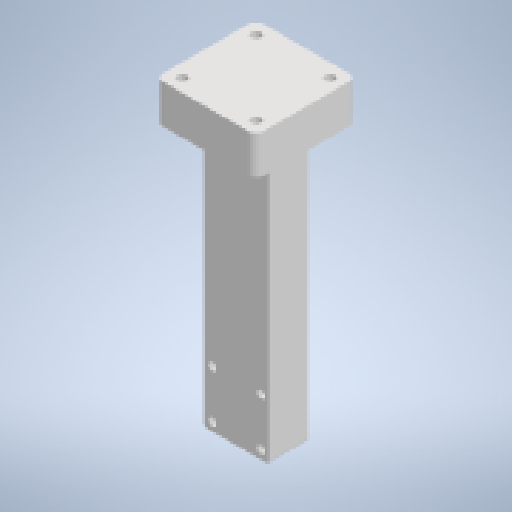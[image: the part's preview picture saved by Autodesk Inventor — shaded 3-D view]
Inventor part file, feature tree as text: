
AUTODESK INVENTOR PART (.ipt)
format: ipt  version: 2023 (Build 270158000, 158)  size: 183,296 bytes
history: native  units: mm
features: sheet_metal_op x3, sketch x2, other x2
ambient origin geometry x8: Origin, YZ Plane, XZ Plane, XY Plane, X Axis, Y Axis, Z Axis, Center Point
bodies: Solid1 (feature_tree)
feature tree (7):
  sheet_metal_op  "Face1"
  sheet_metal_op  "Face2"
  sketch  "Sketch1"  dims[d0=2.0mm]
  other  "Plate1"
  sketch  "Sketch2"  dims[d1=200.0mm d2=25.0mm d3=20.0mm d4=5.0mm d5=5.0mm d7=5.0mm d8=6.0mm d9=25.0mm d10=25.0mm d11=12.5mm d12=50.0mm d13=25.0mm]
  other  "Plate2"
  sheet_metal_op  "Bend1"
